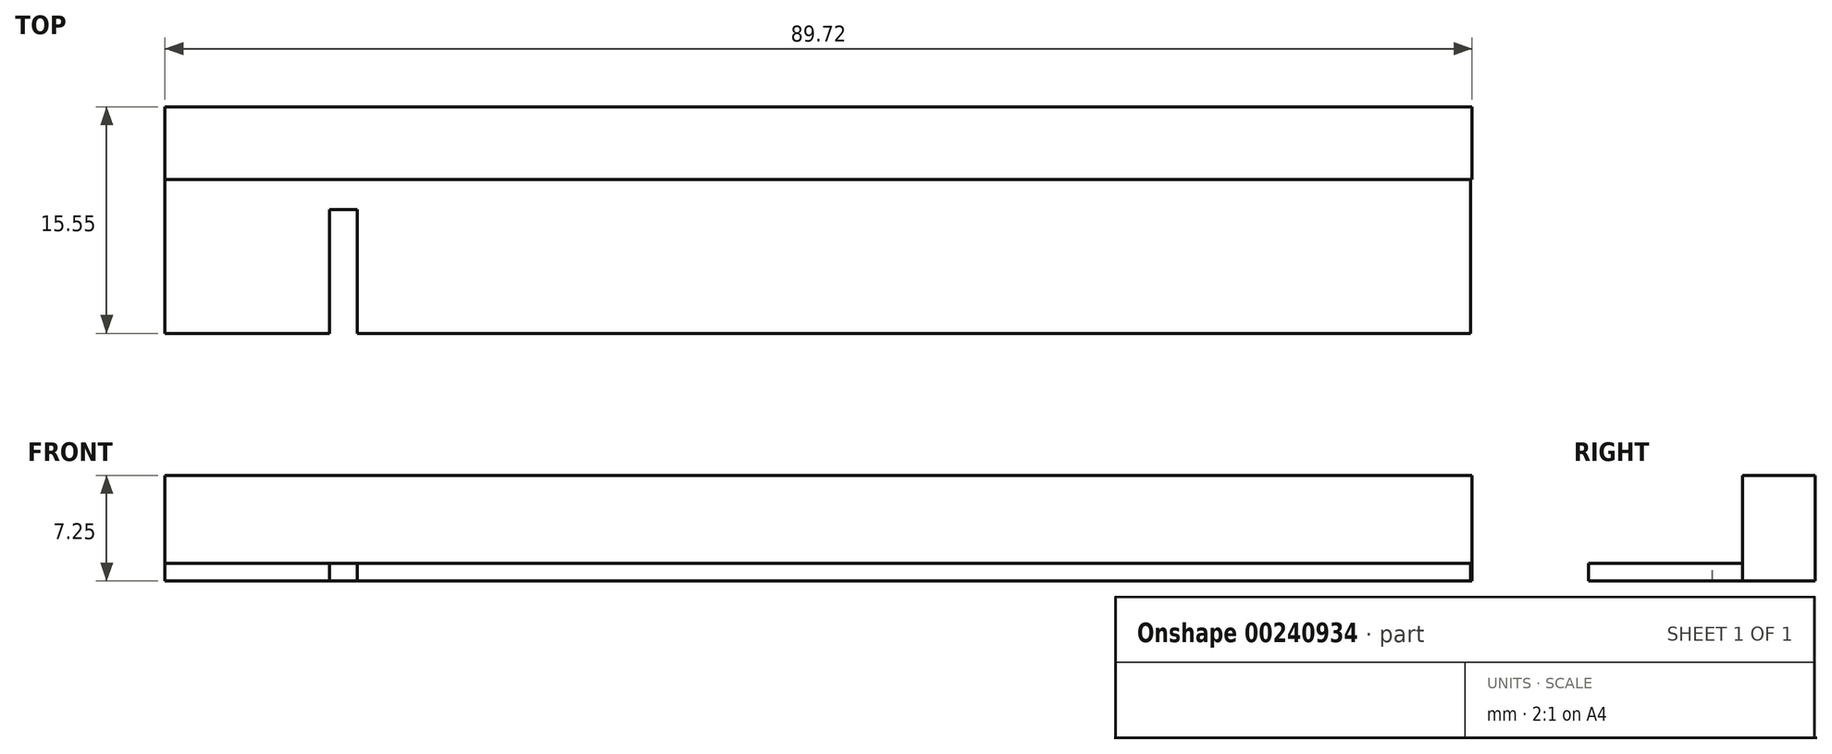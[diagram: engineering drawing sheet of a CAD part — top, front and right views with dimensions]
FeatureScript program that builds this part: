
annotation { "Feature Type Name" : "Feature", "Feature Type Description" : "" }
export const myFeature = defineFeature(function(context is Context, id is Id, definition is map)
    precondition{}
    {
        {
            var Q0;
            Q0=qCreatedBy(makeId("Top.planeOp"),FACE);
            var sketch = newSketch(context, id + "F0", { "sketchPlane" : qUnion([Q0])});
            skLineSegment(sketch, "E0.bottom", {"start": v(76.5, -34.5) * mm, "end": v(-76.5, -34.5) * mm});
            skLineSegment(sketch, "E0.top", {"start": v(76.5, 34.5) * mm, "end": v(-76.5, 34.5) * mm});
            skLineSegment(sketch, "E0.left", {"start": v(76.5, -34.5) * mm, "end": v(76.5, 34.5) * mm});
            skLineSegment(sketch, "E0.right", {"start": v(-76.5, -34.5) * mm, "end": v(-76.5, 34.5) * mm});
            skPoint(sketch, "E0.middle", {"position": v(0, 0) * mm});
            skSolve(sketch);
        }
        {
            var Q0;
            Q0=qSketchRegion(id+"F0",true);
            extrude(context, id + "F1", {"entities" : qUnion([Q0]), "depth" : 1.7 * mm});
        }
        {
            var Q0;
            Q0=makeQuery(id+"F1.opExtrude","CAP_FACE",FACE,{"disambiguationData":[OSD([sQuery(id+"F0.wireOp",EDGE,"E0.bottom"),sQuery(id+"F0.wireOp",EDGE,"E0.top"),sQuery(id+"F0.wireOp",EDGE,"E0.left"),sQuery(id+"F0.wireOp",EDGE,"E0.right")])],"isStart":false});
            var sketch = newSketch(context, id + "F2", { "sketchPlane" : qUnion([Q0])});
            skLineSegment(sketch, "E1.bottom", {"start": v(-76.5, -34.5) * mm, "end": v(-61.5, -34.5) * mm});
            skLineSegment(sketch, "E1.top", {"start": v(-76.5, -29.9) * mm, "end": v(-61.5, -29.9) * mm});
            skLineSegment(sketch, "E1.left", {"start": v(-76.5, -34.5) * mm, "end": v(-76.5, -29.9) * mm});
            skLineSegment(sketch, "E1.right", {"start": v(-61.5, -34.5) * mm, "end": v(-61.5, -29.9) * mm});
            skLineSegment(sketch, "E2.bottom", {"start": v(-61.5, -34.5) * mm, "end": v(-43.1, -34.5) * mm});
            skLineSegment(sketch, "E2.top", {"start": v(-61.5, -21.9) * mm, "end": v(-43.1, -21.9) * mm});
            skLineSegment(sketch, "E2.left", {"start": v(-61.5, -34.5) * mm, "end": v(-61.5, -21.9) * mm});
            skLineSegment(sketch, "E2.right", {"start": v(-43.1, -34.5) * mm, "end": v(-43.1, -21.9) * mm});
            skLineSegment(sketch, "E3.bottom", {"start": v(-43.1, -29.9) * mm, "end": v(-35.1, -29.9) * mm});
            skLineSegment(sketch, "E3.top", {"start": v(-43.1, -34.5) * mm, "end": v(-35.1, -34.5) * mm});
            skLineSegment(sketch, "E3.left", {"start": v(-43.1, -29.9) * mm, "end": v(-43.1, -34.5) * mm});
            skLineSegment(sketch, "E3.right", {"start": v(-35.1, -29.9) * mm, "end": v(-35.1, -34.5) * mm});
            skLineSegment(sketch, "E4.bottom", {"start": v(-35.1, -34.5) * mm, "end": v(-31.6, -34.5) * mm});
            skLineSegment(sketch, "E4.top", {"start": v(-35.1, -21.9) * mm, "end": v(-31.6, -21.9) * mm});
            skLineSegment(sketch, "E4.left", {"start": v(-35.1, -34.5) * mm, "end": v(-35.1, -21.9) * mm});
            skLineSegment(sketch, "E4.right", {"start": v(-31.6, -34.5) * mm, "end": v(-31.6, -21.9) * mm});
            skLineSegment(sketch, "E5", {"start": v(-31.6, -34.5) * mm, "end": v(-20.3, -34.5) * mm, "construction": true});
            skLineSegment(sketch, "E6.bottom", {"start": v(-20.3, -34.5) * mm, "end": v(-18.4, -34.5) * mm});
            skLineSegment(sketch, "E6.top", {"start": v(-20.3, -26) * mm, "end": v(-18.4, -26) * mm});
            skLineSegment(sketch, "E6.left", {"start": v(-20.3, -34.5) * mm, "end": v(-20.3, -26) * mm});
            skLineSegment(sketch, "E6.right", {"start": v(-18.4, -34.5) * mm, "end": v(-18.4, -26) * mm});
            skLineSegment(sketch, "E7", {"start": v(-18.4, -34.5) * mm, "end": v(58, -34.5) * mm, "construction": true});
            skLineSegment(sketch, "E8.bottom", {"start": v(58, -34.5) * mm, "end": v(76.5, -34.5) * mm});
            skLineSegment(sketch, "E8.top", {"start": v(58, -21.9) * mm, "end": v(76.5, -21.9) * mm});
            skLineSegment(sketch, "E8.left", {"start": v(58, -34.5) * mm, "end": v(58, -21.9) * mm});
            skLineSegment(sketch, "E8.right", {"start": v(76.5, -34.5) * mm, "end": v(76.5, -21.9) * mm});
            skLineSegment(sketch, "E9", {"start": v(-69, -29.9) * mm, "end": v(-69, -24.9) * mm, "construction": true});
            skLineSegment(sketch, "E10", {"start": v(-69, -24.9) * mm, "end": v(-76.5, -24.9) * mm, "construction": true});
            skCircle(sketch, "E11", {"center": v(-69, -24.9) * mm, "radius": 2 * mm});
            skLineSegment(sketch, "E12", {"start": v(-69, -24.9) * mm, "end": v(-69, 19.1) * mm, "construction": true});
            skCircle(sketch, "E13", {"center": v(-69, 19.1) * mm, "radius": 2 * mm});
            skLineSegment(sketch, "E14", {"start": v(76.5, 6.3) * mm, "end": v(71.5, 6.3) * mm, "construction": true});
            skLineSegment(sketch, "E15", {"start": v(71.5, -6.2) * mm, "end": v(71.5, 18.8) * mm, "construction": true});
            skLineSegment(sketch, "E16", {"start": v(76.5, 6.3) * mm, "end": v(76.5, -21.9) * mm, "construction": true});
            skCircle(sketch, "E17", {"center": v(71.5, 18.8) * mm, "radius": 1.7 * mm});
            skCircle(sketch, "E18", {"center": v(71.5, -6.2) * mm, "radius": 1.7 * mm});
            skLineSegment(sketch, "E19", {"start": v(71.5, 6.3) * mm, "end": v(41.5, 6.3) * mm, "construction": true});
            skLineSegment(sketch, "E20", {"start": v(41.5, 18.8) * mm, "end": v(41.5, -6.2) * mm, "construction": true});
            skCircle(sketch, "E21", {"center": v(41.5, 18.8) * mm, "radius": 1.7 * mm});
            skCircle(sketch, "E22", {"center": v(41.5, -6.2) * mm, "radius": 1.7 * mm});
            skLineSegment(sketch, "E23", {"start": v(71.5, 18.8) * mm, "end": v(-38.5, 18.8) * mm, "construction": true});
            skLineSegment(sketch, "E24", {"start": v(-38.5, 30.1) * mm, "end": v(-38.5, 7.5) * mm, "construction": true});
            skLineSegment(sketch, "E25.bottom", {"start": v(-41.8, 30.1) * mm, "end": v(-35.2, 30.1) * mm});
            skLineSegment(sketch, "E25.top", {"start": v(-41.8, 28) * mm, "end": v(-35.2, 28) * mm});
            skLineSegment(sketch, "E25.left", {"start": v(-41.8, 30.1) * mm, "end": v(-41.8, 28) * mm});
            skLineSegment(sketch, "E25.right", {"start": v(-35.2, 30.1) * mm, "end": v(-35.2, 28) * mm});
            skLineSegment(sketch, "E26.MirrorCS", {"start": v(-41.8, 9.6) * mm, "end": v(-35.2, 9.6) * mm});
            skLineSegment(sketch, "E27.MirrorCS", {"start": v(-41.8, 7.5) * mm, "end": v(-41.8, 9.6) * mm});
            skLineSegment(sketch, "E28.MirrorCS", {"start": v(-41.8, 7.5) * mm, "end": v(-35.2, 7.5) * mm});
            skLineSegment(sketch, "E29.MirrorCS", {"start": v(-35.2, 7.5) * mm, "end": v(-35.2, 9.6) * mm});
            skLineSegment(sketch, "E30.MirrorCS", {"start": v(-41.8, -17.5) * mm, "end": v(-35.2, -17.5) * mm});
            skLineSegment(sketch, "E31.MirrorCS", {"start": v(-41.8, -17.5) * mm, "end": v(-41.8, -15.4) * mm});
            skLineSegment(sketch, "E32.MirrorCS", {"start": v(-35.2, -17.5) * mm, "end": v(-35.2, -15.4) * mm});
            skLineSegment(sketch, "E33.MirrorCS", {"start": v(-41.8, -15.4) * mm, "end": v(-35.2, -15.4) * mm});
            skLineSegment(sketch, "E34.MirrorCS", {"start": v(-41.8, 3) * mm, "end": v(-35.2, 3) * mm});
            skLineSegment(sketch, "E35.MirrorCS", {"start": v(-41.8, 5.1) * mm, "end": v(-41.8, 3) * mm});
            skLineSegment(sketch, "E36.MirrorCS", {"start": v(-35.2, 5.1) * mm, "end": v(-35.2, 3) * mm});
            skLineSegment(sketch, "E37.MirrorCS", {"start": v(-41.8, 5.1) * mm, "end": v(-35.2, 5.1) * mm});
            skLineSegment(sketch, "E38", {"start": v(16.5, 18.8) * mm, "end": v(16.5, 6.3) * mm, "construction": true});
            skLineSegment(sketch, "E39", {"start": v(16.5, 6.3) * mm, "end": v(11.5, 6.3) * mm, "construction": true});
            skLineSegment(sketch, "E40", {"start": v(11.5, 11.3) * mm, "end": v(11.5, 1.3) * mm, "construction": true});
            skLineSegment(sketch, "E41.MirrorCS", {"start": v(64.8, 30.1) * mm, "end": v(58.2, 30.1) * mm});
            skLineSegment(sketch, "E42.MirrorCS", {"start": v(64.8, 30.1) * mm, "end": v(64.8, 28) * mm});
            skLineSegment(sketch, "E43.MirrorCS", {"start": v(58.2, 30.1) * mm, "end": v(58.2, 28) * mm});
            skLineSegment(sketch, "E44.MirrorCS", {"start": v(64.8, 28) * mm, "end": v(58.2, 28) * mm});
            skLineSegment(sketch, "E45.MirrorCS", {"start": v(64.8, 9.6) * mm, "end": v(58.2, 9.6) * mm});
            skLineSegment(sketch, "E46.MirrorCS", {"start": v(64.8, 7.5) * mm, "end": v(64.8, 9.6) * mm});
            skLineSegment(sketch, "E47.MirrorCS", {"start": v(58.2, 7.5) * mm, "end": v(58.2, 9.6) * mm});
            skLineSegment(sketch, "E48.MirrorCS", {"start": v(64.8, 7.5) * mm, "end": v(58.2, 7.5) * mm});
            skLineSegment(sketch, "E49.MirrorCS", {"start": v(64.8, 5.1) * mm, "end": v(58.2, 5.1) * mm});
            skLineSegment(sketch, "E50.MirrorCS", {"start": v(64.8, 5.1) * mm, "end": v(64.8, 3) * mm});
            skLineSegment(sketch, "E51.MirrorCS", {"start": v(58.2, 5.1) * mm, "end": v(58.2, 3) * mm});
            skLineSegment(sketch, "E52.MirrorCS", {"start": v(64.8, 3) * mm, "end": v(58.2, 3) * mm});
            skLineSegment(sketch, "E53.MirrorCS", {"start": v(64.8, -15.4) * mm, "end": v(58.2, -15.4) * mm});
            skLineSegment(sketch, "E54.MirrorCS", {"start": v(64.8, -17.5) * mm, "end": v(64.8, -15.4) * mm});
            skLineSegment(sketch, "E55.MirrorCS", {"start": v(64.8, -17.5) * mm, "end": v(58.2, -17.5) * mm});
            skLineSegment(sketch, "E56.MirrorCS", {"start": v(58.2, -17.5) * mm, "end": v(58.2, -15.4) * mm});
            skCircle(sketch, "E57.MirrorC", {"center": v(-18.5, 18.8) * mm, "radius": 1.7 * mm});
            skCircle(sketch, "E58.MirrorC", {"center": v(-48.5, 18.8) * mm, "radius": 1.7 * mm});
            skCircle(sketch, "E59.MirrorC", {"center": v(-18.5, -6.2) * mm, "radius": 1.7 * mm});
            skCircle(sketch, "E60.MirrorC", {"center": v(-48.5, -6.2) * mm, "radius": 1.7 * mm});
            skSolve(sketch);
        }
        {
            var Q0;
            Q0=qSketchRegion(id+"F2",true);
            extrude(context, id + "F3", {"entities" : qUnion([Q0]), "operationType" : NewBodyOperationType.REMOVE, "endBound" : BoundingType.THROUGH_ALL, "oppositeDirection" : true, "depth" : 25 * mm});
        }
        {
            var Q0;
            Q0=qCreatedBy(makeId("Top.planeOp"),FACE);
            var sketch = newSketch(context, id + "F4", { "sketchPlane" : qUnion([Q0])});
            skPoint(sketch, "E61.0", {"position": v(-31.6, -21.9) * mm});
            skPoint(sketch, "E62.0", {"position": v(-20.3, -26) * mm});
            skPoint(sketch, "E63.0", {"position": v(-18.4, -26) * mm});
            skPoint(sketch, "E64.0", {"position": v(58, -21.9) * mm});
            skPoint(sketch, "E65.0", {"position": v(-31.6, -34.5) * mm});
            skPoint(sketch, "E66.0", {"position": v(58, -34.5) * mm});
            skLineSegment(sketch, "E67", {"start": v(-31.6, -21.9) * mm, "end": v(-31.6, -26) * mm, "construction": true});
            skLineSegment(sketch, "E68.bottom", {"start": v(-31.6, -23.95) * mm, "end": v(58.12, -23.95) * mm});
            skLineSegment(sketch, "E68.top", {"start": v(-31.6, -18.95) * mm, "end": v(58.12, -18.95) * mm});
            skLineSegment(sketch, "E68.left", {"start": v(-31.6, -23.95) * mm, "end": v(-31.6, -18.95) * mm});
            skLineSegment(sketch, "E68.right", {"start": v(58.12, -23.95) * mm, "end": v(58.12, -18.95) * mm});
            skSolve(sketch);
        }
        {
            var Q0;
            Q0=qSketchRegion(id+"F4",true);
            extrude(context, id + "F5", {"entities" : qUnion([Q0]), "operationType" : NewBodyOperationType.REMOVE, "endBound" : BoundingType.THROUGH_ALL, "depth" : 25 * mm});
        }
        {
            var Q0;
            Q0 = qSketchRegion(id + "F4", true);
            extrude(context, id + "F6", {"entities" : qUnion([Q0]), "operationType" : NewBodyOperationType.ADD, "depth" : 7.25 * mm});
        }
        {
            var Q0;
            Q0=qCreatedBy(makeId("Top.planeOp"),FACE);
            var sketch = newSketch(context, id + "F7", { "sketchPlane" : qUnion([Q0])});
            skLineSegment(sketch, "E69.0", {"start": v(76.5, 34.5) * mm, "end": v(-76.5, 34.5) * mm});
            skLineSegment(sketch, "E70.0", {"start": v(-76.5, -29.9) * mm, "end": v(-76.5, 34.5) * mm});
            skLineSegment(sketch, "E71.0", {"start": v(-76.5, -29.9) * mm, "end": v(-61.5, -29.9) * mm});
            skLineSegment(sketch, "E72.0", {"start": v(-61.5, -29.9) * mm, "end": v(-61.5, -21.9) * mm});
            skLineSegment(sketch, "E73.0", {"start": v(-61.5, -21.9) * mm, "end": v(-43.1, -21.9) * mm});
            skLineSegment(sketch, "E74.0", {"start": v(-43.1, -29.9) * mm, "end": v(-43.1, -21.9) * mm});
            skLineSegment(sketch, "E75.0", {"start": v(-43.1, -29.9) * mm, "end": v(-35.1, -29.9) * mm});
            skLineSegment(sketch, "E76.0", {"start": v(-35.1, -29.9) * mm, "end": v(-35.1, -21.9) * mm});
            skLineSegment(sketch, "E77.0", {"start": v(-35.1, -21.9) * mm, "end": v(-31.6, -21.9) * mm});
            skLineSegment(sketch, "E78.0", {"start": v(-31.6, -18.95) * mm, "end": v(-31.6, -21.9) * mm});
            skLineSegment(sketch, "E79.0", {"start": v(58.12, -18.95) * mm, "end": v(-31.6, -18.95) * mm});
            skLineSegment(sketch, "E80.0", {"start": v(58.12, -18.95) * mm, "end": v(58.12, -21.9) * mm});
            skLineSegment(sketch, "E81.0", {"start": v(58.12, -21.9) * mm, "end": v(76.5, -21.9) * mm});
            skLineSegment(sketch, "E82.0", {"start": v(76.5, -21.9) * mm, "end": v(76.5, 34.5) * mm});
            skSolve(sketch);
        }
        {
            var Q0;
            Q0 = qSketchRegion(id + "F7", true);
            extrude(context, id + "F8", {"entities" : qUnion([Q0]), "operationType" : NewBodyOperationType.REMOVE, "endBound" : BoundingType.THROUGH_ALL, "depth" : 25 * mm});
        }
        {
            var Q0;
            {var subQ0=sQuery(id+"F0.wireOp",EDGE,"E0.bottom");Q0=makeQuery(id+"F5.boolean.opBoolean","SPLIT",FACE,{"disambiguationData":[TD([makeQuery(id+"F1.opExtrude","SWEPT_FACE",FACE,{"disambiguationData":[OSD([subQ0])]})])],"derivedFrom":makeQuery(id+"F1.opExtrude","CAP_FACE",FACE,{"disambiguationData":[OSD([subQ0,sQuery(id+"F0.wireOp",EDGE,"E0.top"),sQuery(id+"F0.wireOp",EDGE,"E0.left"),sQuery(id+"F0.wireOp",EDGE,"E0.right")])],"isStart":false})});}
            extrude(context, id + "F9", {"entities" : qUnion([Q0]), "operationType" : NewBodyOperationType.REMOVE, "oppositeDirection" : true, "depth" : .5 * mm});
        }
    });
